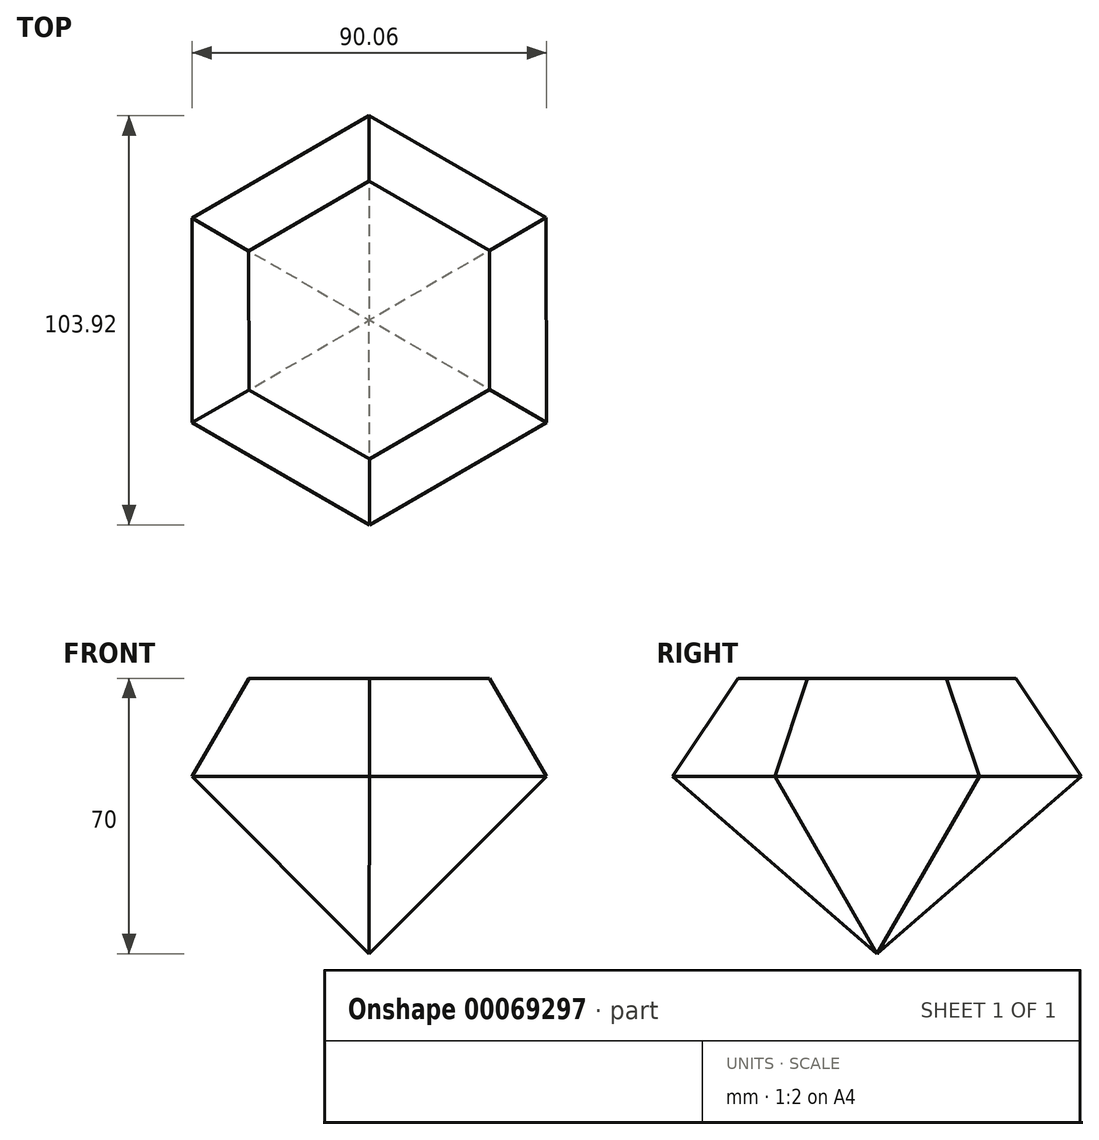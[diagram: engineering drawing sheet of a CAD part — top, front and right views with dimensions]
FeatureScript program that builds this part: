
annotation { "Feature Type Name" : "Feature", "Feature Type Description" : "" }
export const myFeature = defineFeature(function(context is Context, id is Id, definition is map)
    precondition{}
    {
        {
            var Q0;
            Q0=qCreatedBy(makeId("Top.planeOp"),FACE);
            var sketch = newSketch(context, id + "F0", { "sketchPlane" : qUnion([Q0])});
            skCircle(sketch, "E0.cCircle", {"center": v(0, 0) * mm, "radius": 45 * mm, "construction": true});
            skLineSegment(sketch, "E0.0", {"start": v(45.03, -25.92) * mm, "end": v(0.07, -51.96) * mm});
            skLineSegment(sketch, "E0.1", {"start": v(0.07, -51.96) * mm, "end": v(-44.97, -26.04) * mm});
            skLineSegment(sketch, "E0.2", {"start": v(-44.97, -26.04) * mm, "end": v(-45.03, 25.92) * mm});
            skLineSegment(sketch, "E0.3", {"start": v(-45.03, 25.92) * mm, "end": v(-0.07, 51.96) * mm});
            skLineSegment(sketch, "E0.4", {"start": v(-0.07, 51.96) * mm, "end": v(44.97, 26.04) * mm});
            skLineSegment(sketch, "E0.5", {"start": v(44.97, 26.04) * mm, "end": v(45.03, -25.92) * mm});
            skPoint(sketch, "E0.0.midPoint", {"position": v(22.55, -38.94) * mm});
            skSolve(sketch);
        }
        {
            var Q0;
            Q0=makeQuery(id+"F0.imprint","IMPRINT",FACE,{"disambiguationData":[TD([[makeQuery(id+"F0.imprint","IMPRINT",EDGE,{"derivedFrom":sQuery(id+"F0.wireOp",EDGE,"E0.0")}),-1.0]])]});
            extrude(context, id + "F1", {"entities" : qUnion([Q0]), "depth" : 25 * mm, "hasDraft" : true, "draftAngle" : 30 * degree, "draftPullDirection" : true, "hasSecondDirection" : true, "secondDirectionOppositeDirection" : true, "secondDirectionDepth" : 50 * mm, "hasSecondDirectionDraft" : true, "secondDirectionDraftAngle" : 45 * degree, "secondDirectionDraftPullDirection" : true});
        }
    });
